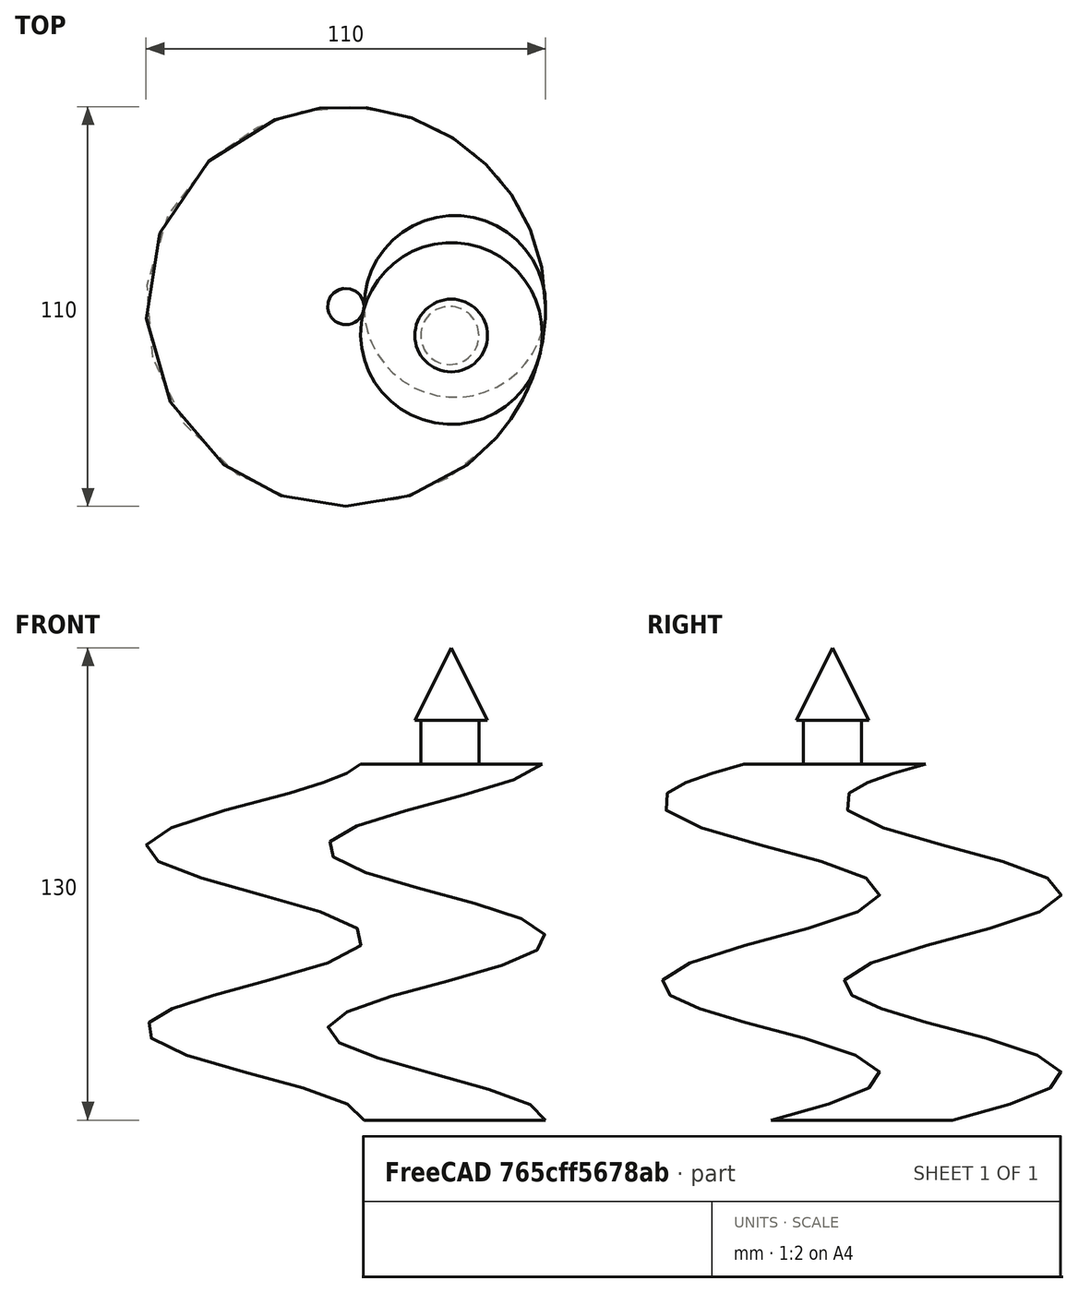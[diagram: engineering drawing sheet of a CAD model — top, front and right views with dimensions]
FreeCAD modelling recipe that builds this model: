
FCSTD DOCUMENT  (FreeCAD 0.15R4671 (Git))
Label: arbitary_wire
License: All rights reserved
LicenseURL: http://en.wikipedia.org/wiki/All_rights_reserved
objects: Part::Feature×3, Part::Part2DObjectPython×1, Part::Cone×1, Part::Cylinder×1, Part::MultiFuse×1, Mesh::Feature×1
note: 7 computed .brp shape members not serialized (recipe doc carries the construction recipe); baked Part::Feature solids carry a one-line shape summary decoded from their .brp

FEATURE [Part::Feature] Shape0_848694915988
  shape: bbox 126.4 x 131 x 98 mm, 3 faces (baked)
FEATURE [Part::Feature] Face
  shape: bbox 8.605 x 34.58 x 2e-07 mm, 1 faces, 0 solids (baked)
FEATURE [Part::Feature] Face001
  shape: bbox 17.16 x 14.86 x 2e-07 mm, 1 faces, 0 solids (baked)
FEATURE [Part::Part2DObjectPython] Fusion  # Draft 2D object (typed FeaturePython)
  Base = -> Face
  ChamferSize = 0
  Closed = false
  End = (6.46898,-22.0115,43)
  FilletRadius = 0
  Length = 0
  MakeFace = true
  Placement = pos=(4.91402,7.18644,43) rot=(0,0,-1;0.785398rad)
  Points = (7) [(26.0236,-19.5466,0),(17.4435,-4.68592,0),(8.86199,-19.5466,0),(13.1405,-19.5466,0),(13.1405,-53.7696,0),(21.7456,-53.7696,0),(21.7456,-19.5466,0)]
  Start = (9.49401,-25.0366,43)
  Tool = -> Face001
FEATURE [Part::Cone] Cone
  Angle = 360
  Height = 20
  Placement = pos=(-1,-8,110) rot=(0,0,1;3.14159rad)
  Radius1 = 10
  Radius2 = 0
FEATURE [Part::Cylinder] Cylinder
  Angle = 360
  Height = 15
  Placement = pos=(-1.4,-8,95) rot=(0,0,1;0rad)
  Radius = 8
FEATURE [Part::MultiFuse] Fusion001
  Shapes = -> [Cone,Cylinder,Shape0_848694915988]
FEATURE [Mesh::Feature] Mesh  label="Fusion001 (Meshed)"
